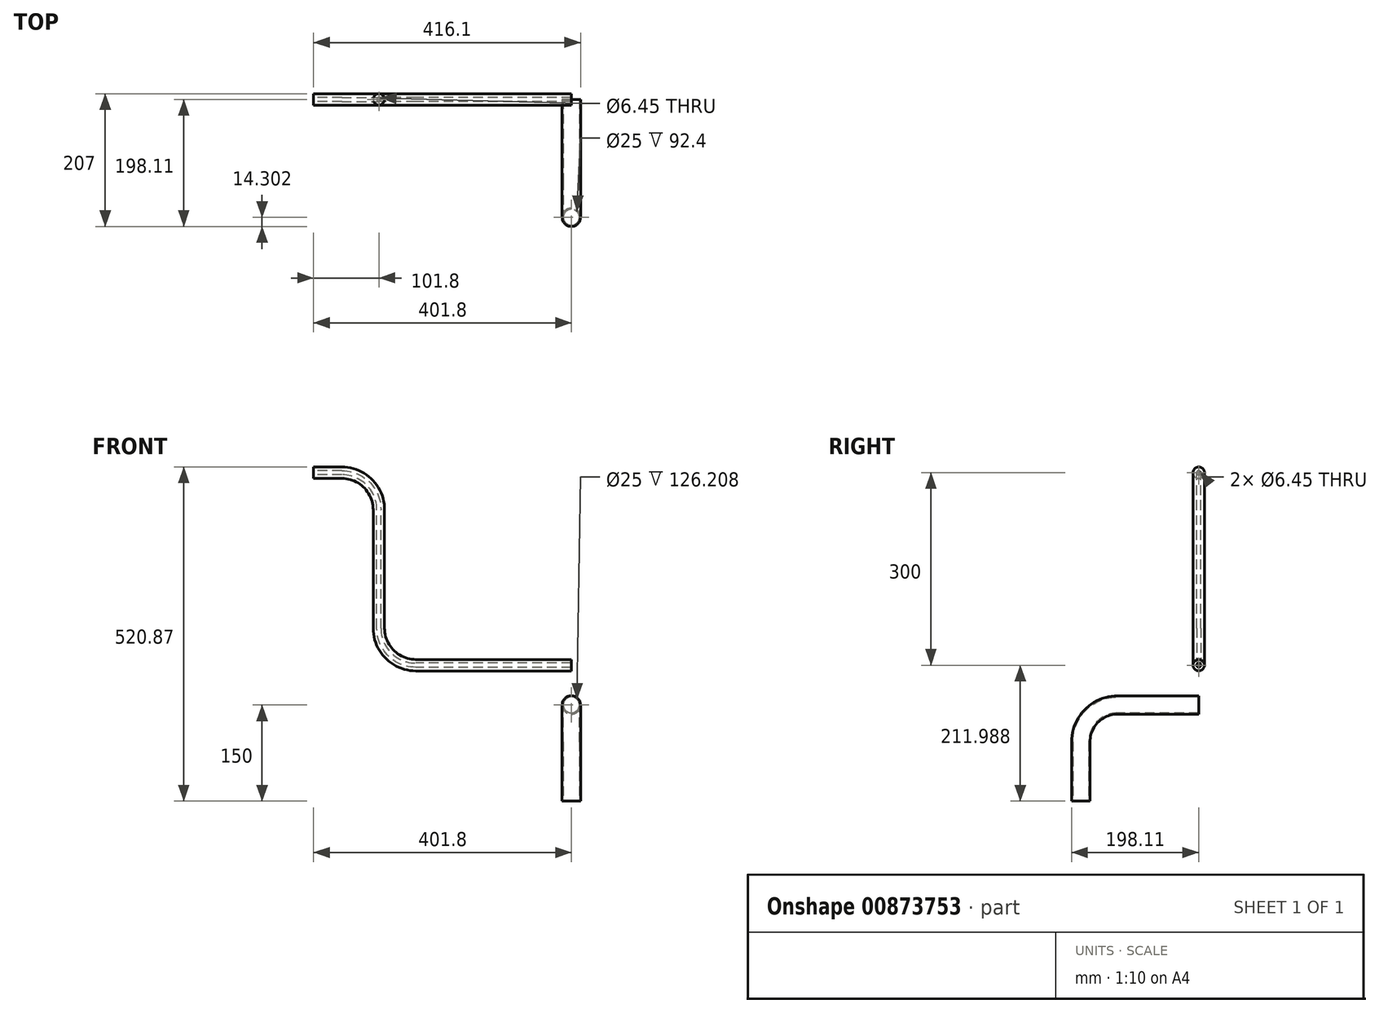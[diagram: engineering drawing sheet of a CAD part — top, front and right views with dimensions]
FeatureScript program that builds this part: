
annotation { "Feature Type Name" : "Feature", "Feature Type Description" : "" }
export const myFeature = defineFeature(function(context is Context, id is Id, definition is map)
    precondition{}
    {
        {
            var Q0;
            Q0=qCreatedBy(makeId("Front.planeOp"),FACE);
            var sketch = newSketch(context, id + "F0", { "sketchPlane" : qUnion([Q0])});
            skCircle(sketch, "E0", {"center": v(0, 0) * mm, "radius": 14.3 * mm});
            skCircle(sketch, "E1", {"center": v(0, 0) * mm, "radius": 12.5 * mm});
            skSolve(sketch);
        }
        {
            var Q0;
            Q0=qCreatedBy(makeId("Right.planeOp"),FACE);
            var sketch = newSketch(context, id + "F1", { "sketchPlane" : qUnion([Q0])});
            skLineSegment(sketch, "E2", {"start": v(0, 0) * mm, "end": v(-126.2, 0) * mm});
            skLineSegment(sketch, "E3", {"start": v(-183.8, -57.6) * mm, "end": v(-183.8, -150) * mm});
            skPoint(sketch, "E4.visualSharp", {"position": v(-183.8, 0) * mm});
            skArc(sketch, "E4.filletArc", {"start": v(-126.2, 0) * mm, "mid": v(-166.94, -16.87) * mm, "end": v(-183.8, -57.6) * mm});
            skSolve(sketch);
        }
        {
            var Q0;
            Q0=makeQuery(id+"F0.imprint","IMPRINT",FACE,{"disambiguationData":[TD([[makeQuery(id+"F0.imprint","IMPRINT",EDGE,{"derivedFrom":sQuery(id+"F0.wireOp",EDGE,"E0")}),1.0]])]});
            var Q1;
            Q1=sQuery(id+"F1.wireOp",EDGE,"E2");
            var Q2;
            Q2=sQuery(id+"F1.wireOp",EDGE,"E4.filletArc");
            var Q3;
            Q3=sQuery(id+"F1.wireOp",EDGE,"E3");
            sweep(context, id + "F2", {"profiles" : qUnion([Q0]), "path" : qUnion([Q1, Q2, Q3])});
        }
        {
            var Q0;
            Q0=qCreatedBy(makeId("Right.planeOp"),FACE);
            var sketch = newSketch(context, id + "F3", { "sketchPlane" : qUnion([Q0])});
            skCircle(sketch, "E5", {"center": v(0, 61.99) * mm, "radius": 8.89 * mm});
            skCircle(sketch, "E6", {"center": v(0, 61.99) * mm, "radius": 3.22 * mm});
            skSolve(sketch);
        }
        {
            var Q0;
            Q0=qCreatedBy(makeId("Front.planeOp"),FACE);
            var sketch = newSketch(context, id + "F4", { "sketchPlane" : qUnion([Q0])});
            skLineSegment(sketch, "E7", {"start": v(0, 61.99) * mm, "end": v(-242.4, 61.99) * mm});
            skLineSegment(sketch, "E8", {"start": v(-300, 119.59) * mm, "end": v(-300, 304.39) * mm});
            skLineSegment(sketch, "E9", {"start": v(-357.6, 361.99) * mm, "end": v(-401.8, 361.99) * mm});
            skPoint(sketch, "E10.visualSharp", {"position": v(-300, 61.99) * mm});
            skArc(sketch, "E10.filletArc", {"start": v(-300, 119.59) * mm, "mid": v(-283.13, 78.86) * mm, "end": v(-242.4, 61.99) * mm});
            skPoint(sketch, "E11.visualSharp", {"position": v(-300, 361.99) * mm});
            skArc(sketch, "E11.filletArc", {"start": v(-300, 304.39) * mm, "mid": v(-316.87, 345.12) * mm, "end": v(-357.6, 361.99) * mm});
            skSolve(sketch);
        }
        {
            var Q0;
            Q0=makeQuery(id+"F3.imprint","IMPRINT",FACE,{"disambiguationData":[TD([[makeQuery(id+"F3.imprint","IMPRINT",EDGE,{"derivedFrom":sQuery(id+"F3.wireOp",EDGE,"E5")}),1.0]])]});
            var Q1;
            Q1=sQuery(id+"F4.wireOp",EDGE,"E7");
            var Q2;
            Q2=sQuery(id+"F4.wireOp",EDGE,"E10.filletArc");
            var Q3;
            Q3=sQuery(id+"F4.wireOp",EDGE,"E8");
            var Q4;
            Q4=sQuery(id+"F4.wireOp",EDGE,"E11.filletArc");
            var Q5;
            Q5=sQuery(id+"F4.wireOp",EDGE,"E9");
            sweep(context, id + "F5", {"profiles" : qUnion([Q0]), "path" : qUnion([Q1, Q2, Q3, Q4, Q5])});
        }
    });
